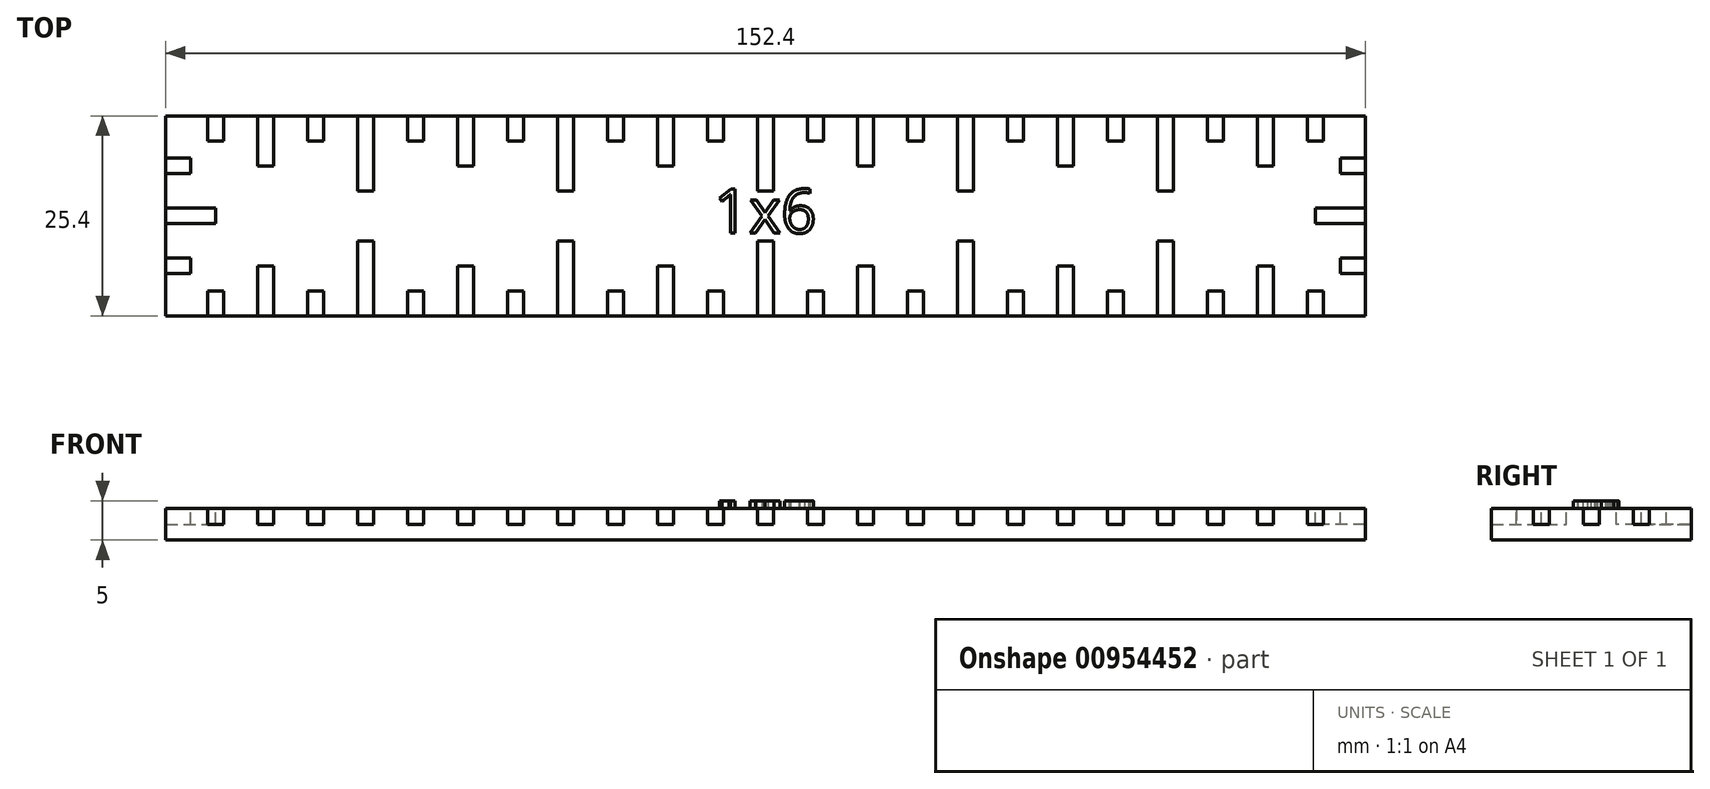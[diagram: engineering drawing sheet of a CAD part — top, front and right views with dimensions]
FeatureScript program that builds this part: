
annotation { "Feature Type Name" : "Feature", "Feature Type Description" : "" }
export const myFeature = defineFeature(function(context is Context, id is Id, definition is map)
    precondition{}
    {
        {
            var Q0;
            Q0=qCreatedBy(makeId("Top.planeOp"),FACE);
            var sketch = newSketch(context, id + "F0", { "sketchPlane" : qUnion([Q0])});
            skLineSegment(sketch, "E0.bottom", {"start": v(-76.2, 12.7) * mm, "end": v(76.2, 12.7) * mm});
            skLineSegment(sketch, "E0.top", {"start": v(-76.2, -12.7) * mm, "end": v(76.2, -12.7) * mm});
            skLineSegment(sketch, "E0.left", {"start": v(-76.2, 12.7) * mm, "end": v(-76.2, -12.7) * mm});
            skLineSegment(sketch, "E0.right", {"start": v(76.2, 12.7) * mm, "end": v(76.2, -12.7) * mm});
            skPoint(sketch, "E0.middle", {"position": v(0, 0) * mm});
            skSolve(sketch);
        }
        {
            var Q0;
            Q0=makeQuery(id+"F0.imprint","IMPRINT",FACE,{"disambiguationData":[TD([[makeQuery(id+"F0.imprint","IMPRINT",EDGE,{"derivedFrom":sQuery(id+"F0.wireOp",EDGE,"E0.bottom")}),-1.0]])]});
            extrude(context, id + "F1", {"entities" : qUnion([Q0]), "depth" : 4 * mm, "offsetDistance" : 25 * mm});
        }
        {
            var Q0;
            Q0=makeQuery(id+"F1.opExtrude","CAP_FACE",FACE,{"disambiguationData":[OSD([sQuery(id+"F0.wireOp",EDGE,"E0.bottom"),sQuery(id+"F0.wireOp",EDGE,"E0.top"),sQuery(id+"F0.wireOp",EDGE,"E0.left"),sQuery(id+"F0.wireOp",EDGE,"E0.right")])],"isStart":false});
            var sketch = newSketch(context, id + "F2", { "sketchPlane" : qUnion([Q0])});
            skLineSegment(sketch, "E1.bottom", {"start": v(-1, -3.17) * mm, "end": v(1, -3.17) * mm});
            skLineSegment(sketch, "E1.top", {"start": v(-1, -22.23) * mm, "end": v(1, -22.23) * mm});
            skLineSegment(sketch, "E1.left", {"start": v(-1, -3.17) * mm, "end": v(-1, -22.23) * mm});
            skLineSegment(sketch, "E1.right", {"start": v(1, -3.17) * mm, "end": v(1, -22.23) * mm});
            skPoint(sketch, "E1.middle", {"position": v(0, -12.7) * mm});
            skLineSegment(sketch, "E2.bottom", {"start": v(5.35, -9.53) * mm, "end": v(7.35, -9.53) * mm});
            skLineSegment(sketch, "E2.top", {"start": v(5.35, -15.88) * mm, "end": v(7.35, -15.88) * mm});
            skLineSegment(sketch, "E2.left", {"start": v(5.35, -9.53) * mm, "end": v(5.35, -15.88) * mm});
            skLineSegment(sketch, "E2.right", {"start": v(7.35, -9.53) * mm, "end": v(7.35, -15.88) * mm});
            skPoint(sketch, "E2.middle", {"position": v(6.35, -12.7) * mm});
            skLineSegment(sketch, "E3.bottom", {"start": v(-7.35, -9.53) * mm, "end": v(-5.35, -9.53) * mm});
            skLineSegment(sketch, "E3.top", {"start": v(-7.35, -15.88) * mm, "end": v(-5.35, -15.88) * mm});
            skLineSegment(sketch, "E3.left", {"start": v(-7.35, -9.53) * mm, "end": v(-7.35, -15.88) * mm});
            skLineSegment(sketch, "E3.right", {"start": v(-5.35, -9.53) * mm, "end": v(-5.35, -15.88) * mm});
            skPoint(sketch, "E3.middle", {"position": v(-6.35, -12.7) * mm});
            skLineSegment(sketch, "E4.bottom", {"start": v(-82.55, -1) * mm, "end": v(-82.55, 1) * mm});
            skLineSegment(sketch, "E4.top", {"start": v(-69.85, -1) * mm, "end": v(-69.85, 1) * mm});
            skLineSegment(sketch, "E4.left", {"start": v(-82.55, -1) * mm, "end": v(-69.85, -1) * mm});
            skLineSegment(sketch, "E4.right", {"start": v(-82.55, 1) * mm, "end": v(-69.85, 1) * mm});
            skPoint(sketch, "E4.middle", {"position": v(-76.2, 0) * mm});
            skLineSegment(sketch, "E5.bottom", {"start": v(-79.38, 5.35) * mm, "end": v(-79.38, 7.35) * mm});
            skLineSegment(sketch, "E5.top", {"start": v(-73.03, 5.35) * mm, "end": v(-73.03, 7.35) * mm});
            skLineSegment(sketch, "E5.left", {"start": v(-79.38, 5.35) * mm, "end": v(-73.03, 5.35) * mm});
            skLineSegment(sketch, "E5.right", {"start": v(-79.38, 7.35) * mm, "end": v(-73.03, 7.35) * mm});
            skPoint(sketch, "E5.middle", {"position": v(-76.2, 6.35) * mm});
            skLineSegment(sketch, "E6.bottom", {"start": v(-79.38, -7.35) * mm, "end": v(-79.38, -5.35) * mm});
            skLineSegment(sketch, "E6.top", {"start": v(-73.03, -7.35) * mm, "end": v(-73.03, -5.35) * mm});
            skLineSegment(sketch, "E6.left", {"start": v(-79.38, -7.35) * mm, "end": v(-73.03, -7.35) * mm});
            skLineSegment(sketch, "E6.right", {"start": v(-79.38, -5.35) * mm, "end": v(-73.03, -5.35) * mm});
            skPoint(sketch, "E6.middle", {"position": v(-76.2, -6.35) * mm});
            skLineSegment(sketch, "E7.bottom", {"start": v(1, 3.17) * mm, "end": v(-1, 3.17) * mm});
            skLineSegment(sketch, "E7.top", {"start": v(1, 22.22) * mm, "end": v(-1, 22.22) * mm});
            skLineSegment(sketch, "E7.left", {"start": v(1, 3.17) * mm, "end": v(1, 22.22) * mm});
            skLineSegment(sketch, "E7.right", {"start": v(-1, 3.17) * mm, "end": v(-1, 22.22) * mm});
            skPoint(sketch, "E7.middle", {"position": v(0, 12.7) * mm});
            skLineSegment(sketch, "E8.bottom", {"start": v(-5.35, 9.53) * mm, "end": v(-7.35, 9.53) * mm});
            skLineSegment(sketch, "E8.top", {"start": v(-5.35, 15.88) * mm, "end": v(-7.35, 15.88) * mm});
            skLineSegment(sketch, "E8.left", {"start": v(-5.35, 9.53) * mm, "end": v(-5.35, 15.88) * mm});
            skLineSegment(sketch, "E8.right", {"start": v(-7.35, 9.53) * mm, "end": v(-7.35, 15.88) * mm});
            skPoint(sketch, "E8.middle", {"position": v(-6.35, 12.7) * mm});
            skLineSegment(sketch, "E9.bottom", {"start": v(7.35, 9.52) * mm, "end": v(5.35, 9.52) * mm});
            skLineSegment(sketch, "E9.top", {"start": v(7.35, 15.88) * mm, "end": v(5.35, 15.88) * mm});
            skLineSegment(sketch, "E9.left", {"start": v(7.35, 9.52) * mm, "end": v(7.35, 15.88) * mm});
            skLineSegment(sketch, "E9.right", {"start": v(5.35, 9.52) * mm, "end": v(5.35, 15.88) * mm});
            skPoint(sketch, "E9.middle", {"position": v(6.35, 12.7) * mm});
            skLineSegment(sketch, "E10.bottom", {"start": v(82.55, 1) * mm, "end": v(82.55, -1) * mm});
            skLineSegment(sketch, "E10.top", {"start": v(69.85, 1) * mm, "end": v(69.85, -1) * mm});
            skLineSegment(sketch, "E10.left", {"start": v(82.55, 1) * mm, "end": v(69.85, 1) * mm});
            skLineSegment(sketch, "E10.right", {"start": v(82.55, -1) * mm, "end": v(69.85, -1) * mm});
            skPoint(sketch, "E10.middle", {"position": v(76.2, 0) * mm});
            skLineSegment(sketch, "E11.bottom", {"start": v(79.38, -5.35) * mm, "end": v(79.38, -7.35) * mm});
            skLineSegment(sketch, "E11.top", {"start": v(73.03, -5.35) * mm, "end": v(73.03, -7.35) * mm});
            skLineSegment(sketch, "E11.left", {"start": v(79.38, -5.35) * mm, "end": v(73.03, -5.35) * mm});
            skLineSegment(sketch, "E11.right", {"start": v(79.38, -7.35) * mm, "end": v(73.03, -7.35) * mm});
            skPoint(sketch, "E11.middle", {"position": v(76.2, -6.35) * mm});
            skLineSegment(sketch, "E12.bottom", {"start": v(79.38, 7.35) * mm, "end": v(79.38, 5.35) * mm});
            skLineSegment(sketch, "E12.top", {"start": v(73.03, 7.35) * mm, "end": v(73.03, 5.35) * mm});
            skLineSegment(sketch, "E12.left", {"start": v(79.38, 7.35) * mm, "end": v(73.03, 7.35) * mm});
            skLineSegment(sketch, "E12.right", {"start": v(79.38, 5.35) * mm, "end": v(73.03, 5.35) * mm});
            skPoint(sketch, "E12.middle", {"position": v(76.2, 6.35) * mm});
            skLineSegment(sketch, "E13.bottom", {"start": v(-11.7, 6.35) * mm, "end": v(-13.7, 6.35) * mm});
            skLineSegment(sketch, "E13.top", {"start": v(-11.7, 19.05) * mm, "end": v(-13.7, 19.05) * mm});
            skLineSegment(sketch, "E13.left", {"start": v(-11.7, 6.35) * mm, "end": v(-11.7, 19.05) * mm});
            skLineSegment(sketch, "E13.right", {"start": v(-13.7, 6.35) * mm, "end": v(-13.7, 19.05) * mm});
            skPoint(sketch, "E13.middle", {"position": v(-12.7, 12.7) * mm});
            skLineSegment(sketch, "E14.bottom", {"start": v(-18.05, 9.53) * mm, "end": v(-20.05, 9.53) * mm});
            skLineSegment(sketch, "E14.top", {"start": v(-18.05, 15.88) * mm, "end": v(-20.05, 15.88) * mm});
            skLineSegment(sketch, "E14.left", {"start": v(-18.05, 9.53) * mm, "end": v(-18.05, 15.88) * mm});
            skLineSegment(sketch, "E14.right", {"start": v(-20.05, 9.53) * mm, "end": v(-20.05, 15.88) * mm});
            skPoint(sketch, "E14.middle", {"position": v(-19.05, 12.7) * mm});
            skLineSegment(sketch, "E15.bottom", {"start": v(-11.7, -19.05) * mm, "end": v(-13.7, -19.05) * mm});
            skLineSegment(sketch, "E15.top", {"start": v(-11.7, -6.35) * mm, "end": v(-13.7, -6.35) * mm});
            skLineSegment(sketch, "E15.left", {"start": v(-11.7, -19.05) * mm, "end": v(-11.7, -6.35) * mm});
            skLineSegment(sketch, "E15.right", {"start": v(-13.7, -19.05) * mm, "end": v(-13.7, -6.35) * mm});
            skPoint(sketch, "E15.middle", {"position": v(-12.7, -12.7) * mm});
            skLineSegment(sketch, "E16.bottom", {"start": v(-18.05, -15.88) * mm, "end": v(-20.05, -15.88) * mm});
            skLineSegment(sketch, "E16.top", {"start": v(-18.05, -9.53) * mm, "end": v(-20.05, -9.53) * mm});
            skLineSegment(sketch, "E16.left", {"start": v(-18.05, -15.88) * mm, "end": v(-18.05, -9.53) * mm});
            skLineSegment(sketch, "E16.right", {"start": v(-20.05, -15.88) * mm, "end": v(-20.05, -9.53) * mm});
            skPoint(sketch, "E16.middle", {"position": v(-19.05, -12.7) * mm});
            skLineSegment(sketch, "E17.bottom", {"start": v(-5.35, -15.88) * mm, "end": v(-7.35, -15.88) * mm});
            skLineSegment(sketch, "E17.top", {"start": v(-5.35, -9.53) * mm, "end": v(-7.35, -9.53) * mm});
            skLineSegment(sketch, "E17.left", {"start": v(-5.35, -15.88) * mm, "end": v(-5.35, -9.53) * mm});
            skLineSegment(sketch, "E17.right", {"start": v(-7.35, -15.88) * mm, "end": v(-7.35, -9.53) * mm});
            skLineSegment(sketch, "E18.bottom", {"start": v(11.7, -6.35) * mm, "end": v(13.7, -6.35) * mm});
            skLineSegment(sketch, "E18.top", {"start": v(11.7, -19.05) * mm, "end": v(13.7, -19.05) * mm});
            skLineSegment(sketch, "E18.left", {"start": v(11.7, -6.35) * mm, "end": v(11.7, -19.05) * mm});
            skLineSegment(sketch, "E18.right", {"start": v(13.7, -6.35) * mm, "end": v(13.7, -19.05) * mm});
            skPoint(sketch, "E18.middle", {"position": v(12.7, -12.7) * mm});
            skLineSegment(sketch, "E19.bottom", {"start": v(18.05, -9.53) * mm, "end": v(20.05, -9.53) * mm});
            skLineSegment(sketch, "E19.top", {"start": v(18.05, -15.88) * mm, "end": v(20.05, -15.88) * mm});
            skLineSegment(sketch, "E19.left", {"start": v(18.05, -9.53) * mm, "end": v(18.05, -15.88) * mm});
            skLineSegment(sketch, "E19.right", {"start": v(20.05, -9.53) * mm, "end": v(20.05, -15.88) * mm});
            skPoint(sketch, "E19.middle", {"position": v(19.05, -12.7) * mm});
            skLineSegment(sketch, "E20.bottom", {"start": v(11.7, 19.05) * mm, "end": v(13.7, 19.05) * mm});
            skLineSegment(sketch, "E20.top", {"start": v(11.7, 6.35) * mm, "end": v(13.7, 6.35) * mm});
            skLineSegment(sketch, "E20.left", {"start": v(11.7, 19.05) * mm, "end": v(11.7, 6.35) * mm});
            skLineSegment(sketch, "E20.right", {"start": v(13.7, 19.05) * mm, "end": v(13.7, 6.35) * mm});
            skPoint(sketch, "E20.middle", {"position": v(12.7, 12.7) * mm});
            skLineSegment(sketch, "E21.bottom", {"start": v(18.05, 15.88) * mm, "end": v(20.05, 15.88) * mm});
            skLineSegment(sketch, "E21.top", {"start": v(18.05, 9.53) * mm, "end": v(20.05, 9.53) * mm});
            skLineSegment(sketch, "E21.left", {"start": v(18.05, 15.88) * mm, "end": v(18.05, 9.53) * mm});
            skLineSegment(sketch, "E21.right", {"start": v(20.05, 15.88) * mm, "end": v(20.05, 9.53) * mm});
            skPoint(sketch, "E21.middle", {"position": v(19.05, 12.7) * mm});
            skLineSegment(sketch, "E22.bottom", {"start": v(5.35, 15.88) * mm, "end": v(7.35, 15.88) * mm});
            skLineSegment(sketch, "E22.top", {"start": v(5.35, 9.53) * mm, "end": v(7.35, 9.53) * mm});
            skLineSegment(sketch, "E22.left", {"start": v(5.35, 15.88) * mm, "end": v(5.35, 9.53) * mm});
            skLineSegment(sketch, "E22.right", {"start": v(7.35, 15.88) * mm, "end": v(7.35, 9.53) * mm});
            skLineSegment(sketch, "E23.bottom", {"start": v(26.4, 3.17) * mm, "end": v(24.4, 3.17) * mm});
            skLineSegment(sketch, "E23.top", {"start": v(26.4, 22.22) * mm, "end": v(24.4, 22.22) * mm});
            skLineSegment(sketch, "E23.left", {"start": v(26.4, 3.17) * mm, "end": v(26.4, 22.22) * mm});
            skLineSegment(sketch, "E23.right", {"start": v(24.4, 3.17) * mm, "end": v(24.4, 22.22) * mm});
            skPoint(sketch, "E23.middle", {"position": v(25.4, 12.7) * mm});
            skLineSegment(sketch, "E24.bottom", {"start": v(20.05, 9.52) * mm, "end": v(18.05, 9.52) * mm});
            skLineSegment(sketch, "E24.top", {"start": v(20.05, 15.87) * mm, "end": v(18.05, 15.87) * mm});
            skLineSegment(sketch, "E24.left", {"start": v(20.05, 9.52) * mm, "end": v(20.05, 15.87) * mm});
            skLineSegment(sketch, "E24.right", {"start": v(18.05, 9.52) * mm, "end": v(18.05, 15.87) * mm});
            skLineSegment(sketch, "E25.bottom", {"start": v(32.75, 9.52) * mm, "end": v(30.75, 9.52) * mm});
            skLineSegment(sketch, "E25.top", {"start": v(32.75, 15.87) * mm, "end": v(30.75, 15.87) * mm});
            skLineSegment(sketch, "E25.left", {"start": v(32.75, 9.52) * mm, "end": v(32.75, 15.87) * mm});
            skLineSegment(sketch, "E25.right", {"start": v(30.75, 9.52) * mm, "end": v(30.75, 15.87) * mm});
            skPoint(sketch, "E25.middle", {"position": v(31.75, 12.7) * mm});
            skLineSegment(sketch, "E26.bottom", {"start": v(20.05, 9.53) * mm, "end": v(18.05, 9.53) * mm});
            skLineSegment(sketch, "E26.top", {"start": v(20.05, 15.88) * mm, "end": v(18.05, 15.88) * mm});
            skLineSegment(sketch, "E26.left", {"start": v(20.05, 9.53) * mm, "end": v(20.05, 15.88) * mm});
            skLineSegment(sketch, "E26.right", {"start": v(18.05, 9.53) * mm, "end": v(18.05, 15.88) * mm});
            skLineSegment(sketch, "E27.bottom", {"start": v(37.1, 19.05) * mm, "end": v(39.1, 19.05) * mm});
            skLineSegment(sketch, "E27.top", {"start": v(37.1, 6.35) * mm, "end": v(39.1, 6.35) * mm});
            skLineSegment(sketch, "E27.left", {"start": v(37.1, 19.05) * mm, "end": v(37.1, 6.35) * mm});
            skLineSegment(sketch, "E27.right", {"start": v(39.1, 19.05) * mm, "end": v(39.1, 6.35) * mm});
            skPoint(sketch, "E27.middle", {"position": v(38.1, 12.7) * mm});
            skLineSegment(sketch, "E28.bottom", {"start": v(43.45, 15.87) * mm, "end": v(45.45, 15.87) * mm});
            skLineSegment(sketch, "E28.top", {"start": v(43.45, 9.52) * mm, "end": v(45.45, 9.52) * mm});
            skLineSegment(sketch, "E28.left", {"start": v(43.45, 15.87) * mm, "end": v(43.45, 9.52) * mm});
            skLineSegment(sketch, "E28.right", {"start": v(45.45, 15.87) * mm, "end": v(45.45, 9.52) * mm});
            skPoint(sketch, "E28.middle", {"position": v(44.45, 12.7) * mm});
            skLineSegment(sketch, "E29.bottom", {"start": v(30.75, 15.87) * mm, "end": v(32.75, 15.87) * mm});
            skLineSegment(sketch, "E29.top", {"start": v(30.75, 9.52) * mm, "end": v(32.75, 9.52) * mm});
            skLineSegment(sketch, "E29.left", {"start": v(30.75, 15.87) * mm, "end": v(30.75, 9.52) * mm});
            skLineSegment(sketch, "E29.right", {"start": v(32.75, 15.87) * mm, "end": v(32.75, 9.52) * mm});
            skLineSegment(sketch, "E30.bottom", {"start": v(26.4, -22.22) * mm, "end": v(24.4, -22.22) * mm});
            skLineSegment(sketch, "E30.top", {"start": v(26.4, -3.17) * mm, "end": v(24.4, -3.17) * mm});
            skLineSegment(sketch, "E30.left", {"start": v(26.4, -22.22) * mm, "end": v(26.4, -3.17) * mm});
            skLineSegment(sketch, "E30.right", {"start": v(24.4, -22.22) * mm, "end": v(24.4, -3.17) * mm});
            skPoint(sketch, "E30.middle", {"position": v(25.4, -12.7) * mm});
            skLineSegment(sketch, "E31.bottom", {"start": v(20.05, -15.87) * mm, "end": v(18.05, -15.87) * mm});
            skLineSegment(sketch, "E31.top", {"start": v(20.05, -9.52) * mm, "end": v(18.05, -9.52) * mm});
            skLineSegment(sketch, "E31.left", {"start": v(20.05, -15.87) * mm, "end": v(20.05, -9.52) * mm});
            skLineSegment(sketch, "E31.right", {"start": v(18.05, -15.87) * mm, "end": v(18.05, -9.52) * mm});
            skLineSegment(sketch, "E32.bottom", {"start": v(32.75, -15.87) * mm, "end": v(30.75, -15.87) * mm});
            skLineSegment(sketch, "E32.top", {"start": v(32.75, -9.52) * mm, "end": v(30.75, -9.52) * mm});
            skLineSegment(sketch, "E32.left", {"start": v(32.75, -15.87) * mm, "end": v(32.75, -9.52) * mm});
            skLineSegment(sketch, "E32.right", {"start": v(30.75, -15.87) * mm, "end": v(30.75, -9.52) * mm});
            skPoint(sketch, "E32.middle", {"position": v(31.75, -12.7) * mm});
            skLineSegment(sketch, "E33.bottom", {"start": v(37.1, -6.35) * mm, "end": v(39.1, -6.35) * mm});
            skLineSegment(sketch, "E33.top", {"start": v(37.1, -19.05) * mm, "end": v(39.1, -19.05) * mm});
            skLineSegment(sketch, "E33.left", {"start": v(37.1, -6.35) * mm, "end": v(37.1, -19.05) * mm});
            skLineSegment(sketch, "E33.right", {"start": v(39.1, -6.35) * mm, "end": v(39.1, -19.05) * mm});
            skPoint(sketch, "E33.middle", {"position": v(38.1, -12.7) * mm});
            skLineSegment(sketch, "E34.bottom", {"start": v(43.45, -9.52) * mm, "end": v(45.45, -9.52) * mm});
            skLineSegment(sketch, "E34.top", {"start": v(43.45, -15.87) * mm, "end": v(45.45, -15.87) * mm});
            skLineSegment(sketch, "E34.left", {"start": v(43.45, -9.52) * mm, "end": v(43.45, -15.87) * mm});
            skLineSegment(sketch, "E34.right", {"start": v(45.45, -9.52) * mm, "end": v(45.45, -15.87) * mm});
            skPoint(sketch, "E34.middle", {"position": v(44.45, -12.7) * mm});
            skLineSegment(sketch, "E35.bottom", {"start": v(30.75, -9.52) * mm, "end": v(32.75, -9.52) * mm});
            skLineSegment(sketch, "E35.top", {"start": v(30.75, -15.87) * mm, "end": v(32.75, -15.87) * mm});
            skLineSegment(sketch, "E35.left", {"start": v(30.75, -9.52) * mm, "end": v(30.75, -15.87) * mm});
            skLineSegment(sketch, "E35.right", {"start": v(32.75, -9.52) * mm, "end": v(32.75, -15.87) * mm});
            skLineSegment(sketch, "E36.bottom", {"start": v(-26.4, -3.17) * mm, "end": v(-24.4, -3.17) * mm});
            skLineSegment(sketch, "E36.top", {"start": v(-26.4, -22.22) * mm, "end": v(-24.4, -22.22) * mm});
            skLineSegment(sketch, "E36.left", {"start": v(-26.4, -3.17) * mm, "end": v(-26.4, -22.22) * mm});
            skLineSegment(sketch, "E36.right", {"start": v(-24.4, -3.17) * mm, "end": v(-24.4, -22.22) * mm});
            skPoint(sketch, "E36.middle", {"position": v(-25.4, -12.7) * mm});
            skLineSegment(sketch, "E37.bottom", {"start": v(-20.05, -9.52) * mm, "end": v(-18.05, -9.52) * mm});
            skLineSegment(sketch, "E37.top", {"start": v(-20.05, -15.87) * mm, "end": v(-18.05, -15.87) * mm});
            skLineSegment(sketch, "E37.left", {"start": v(-20.05, -9.52) * mm, "end": v(-20.05, -15.87) * mm});
            skLineSegment(sketch, "E37.right", {"start": v(-18.05, -9.52) * mm, "end": v(-18.05, -15.87) * mm});
            skLineSegment(sketch, "E38.bottom", {"start": v(-32.75, -9.52) * mm, "end": v(-30.75, -9.52) * mm});
            skLineSegment(sketch, "E38.top", {"start": v(-32.75, -15.87) * mm, "end": v(-30.75, -15.87) * mm});
            skLineSegment(sketch, "E38.left", {"start": v(-32.75, -9.52) * mm, "end": v(-32.75, -15.87) * mm});
            skLineSegment(sketch, "E38.right", {"start": v(-30.75, -9.52) * mm, "end": v(-30.75, -15.87) * mm});
            skPoint(sketch, "E38.middle", {"position": v(-31.75, -12.7) * mm});
            skLineSegment(sketch, "E39.bottom", {"start": v(-20.05, -9.53) * mm, "end": v(-18.05, -9.53) * mm});
            skLineSegment(sketch, "E39.top", {"start": v(-20.05, -15.88) * mm, "end": v(-18.05, -15.88) * mm});
            skLineSegment(sketch, "E39.left", {"start": v(-20.05, -9.53) * mm, "end": v(-20.05, -15.88) * mm});
            skLineSegment(sketch, "E39.right", {"start": v(-18.05, -9.53) * mm, "end": v(-18.05, -15.88) * mm});
            skLineSegment(sketch, "E40.bottom", {"start": v(-37.1, -19.05) * mm, "end": v(-39.1, -19.05) * mm});
            skLineSegment(sketch, "E40.top", {"start": v(-37.1, -6.35) * mm, "end": v(-39.1, -6.35) * mm});
            skLineSegment(sketch, "E40.left", {"start": v(-37.1, -19.05) * mm, "end": v(-37.1, -6.35) * mm});
            skLineSegment(sketch, "E40.right", {"start": v(-39.1, -19.05) * mm, "end": v(-39.1, -6.35) * mm});
            skPoint(sketch, "E40.middle", {"position": v(-38.1, -12.7) * mm});
            skLineSegment(sketch, "E41.bottom", {"start": v(-43.45, -15.87) * mm, "end": v(-45.45, -15.87) * mm});
            skLineSegment(sketch, "E41.top", {"start": v(-43.45, -9.52) * mm, "end": v(-45.45, -9.52) * mm});
            skLineSegment(sketch, "E41.left", {"start": v(-43.45, -15.87) * mm, "end": v(-43.45, -9.52) * mm});
            skLineSegment(sketch, "E41.right", {"start": v(-45.45, -15.87) * mm, "end": v(-45.45, -9.52) * mm});
            skPoint(sketch, "E41.middle", {"position": v(-44.45, -12.7) * mm});
            skLineSegment(sketch, "E42.bottom", {"start": v(-30.75, -15.87) * mm, "end": v(-32.75, -15.87) * mm});
            skLineSegment(sketch, "E42.top", {"start": v(-30.75, -9.52) * mm, "end": v(-32.75, -9.52) * mm});
            skLineSegment(sketch, "E42.left", {"start": v(-30.75, -15.87) * mm, "end": v(-30.75, -9.52) * mm});
            skLineSegment(sketch, "E42.right", {"start": v(-32.75, -15.87) * mm, "end": v(-32.75, -9.52) * mm});
            skLineSegment(sketch, "E43.bottom", {"start": v(-26.4, 22.22) * mm, "end": v(-24.4, 22.22) * mm});
            skLineSegment(sketch, "E43.top", {"start": v(-26.4, 3.17) * mm, "end": v(-24.4, 3.17) * mm});
            skLineSegment(sketch, "E43.left", {"start": v(-26.4, 22.22) * mm, "end": v(-26.4, 3.17) * mm});
            skLineSegment(sketch, "E43.right", {"start": v(-24.4, 22.22) * mm, "end": v(-24.4, 3.17) * mm});
            skPoint(sketch, "E43.middle", {"position": v(-25.4, 12.7) * mm});
            skLineSegment(sketch, "E44.bottom", {"start": v(-20.05, 15.87) * mm, "end": v(-18.05, 15.87) * mm});
            skLineSegment(sketch, "E44.top", {"start": v(-20.05, 9.52) * mm, "end": v(-18.05, 9.52) * mm});
            skLineSegment(sketch, "E44.left", {"start": v(-20.05, 15.87) * mm, "end": v(-20.05, 9.52) * mm});
            skLineSegment(sketch, "E44.right", {"start": v(-18.05, 15.87) * mm, "end": v(-18.05, 9.52) * mm});
            skLineSegment(sketch, "E45.bottom", {"start": v(-32.75, 15.87) * mm, "end": v(-30.75, 15.87) * mm});
            skLineSegment(sketch, "E45.top", {"start": v(-32.75, 9.52) * mm, "end": v(-30.75, 9.52) * mm});
            skLineSegment(sketch, "E45.left", {"start": v(-32.75, 15.87) * mm, "end": v(-32.75, 9.52) * mm});
            skLineSegment(sketch, "E45.right", {"start": v(-30.75, 15.87) * mm, "end": v(-30.75, 9.52) * mm});
            skPoint(sketch, "E45.middle", {"position": v(-31.75, 12.7) * mm});
            skLineSegment(sketch, "E46.bottom", {"start": v(-37.1, 6.35) * mm, "end": v(-39.1, 6.35) * mm});
            skLineSegment(sketch, "E46.top", {"start": v(-37.1, 19.05) * mm, "end": v(-39.1, 19.05) * mm});
            skLineSegment(sketch, "E46.left", {"start": v(-37.1, 6.35) * mm, "end": v(-37.1, 19.05) * mm});
            skLineSegment(sketch, "E46.right", {"start": v(-39.1, 6.35) * mm, "end": v(-39.1, 19.05) * mm});
            skPoint(sketch, "E46.middle", {"position": v(-38.1, 12.7) * mm});
            skLineSegment(sketch, "E47.bottom", {"start": v(-43.45, 9.52) * mm, "end": v(-45.45, 9.52) * mm});
            skLineSegment(sketch, "E47.top", {"start": v(-43.45, 15.87) * mm, "end": v(-45.45, 15.87) * mm});
            skLineSegment(sketch, "E47.left", {"start": v(-43.45, 9.52) * mm, "end": v(-43.45, 15.87) * mm});
            skLineSegment(sketch, "E47.right", {"start": v(-45.45, 9.52) * mm, "end": v(-45.45, 15.87) * mm});
            skPoint(sketch, "E47.middle", {"position": v(-44.45, 12.7) * mm});
            skLineSegment(sketch, "E48.bottom", {"start": v(-30.75, 9.52) * mm, "end": v(-32.75, 9.52) * mm});
            skLineSegment(sketch, "E48.top", {"start": v(-30.75, 15.87) * mm, "end": v(-32.75, 15.87) * mm});
            skLineSegment(sketch, "E48.left", {"start": v(-30.75, 9.52) * mm, "end": v(-30.75, 15.87) * mm});
            skLineSegment(sketch, "E48.right", {"start": v(-32.75, 9.52) * mm, "end": v(-32.75, 15.87) * mm});
            skLineSegment(sketch, "E49.bottom", {"start": v(43.45, 15.88) * mm, "end": v(45.45, 15.88) * mm});
            skLineSegment(sketch, "E49.top", {"start": v(43.45, 9.53) * mm, "end": v(45.45, 9.53) * mm});
            skLineSegment(sketch, "E49.left", {"start": v(43.45, 15.88) * mm, "end": v(43.45, 9.53) * mm});
            skLineSegment(sketch, "E49.right", {"start": v(45.45, 15.88) * mm, "end": v(45.45, 9.53) * mm});
            skLineSegment(sketch, "E50.bottom", {"start": v(51.8, 3.17) * mm, "end": v(49.8, 3.17) * mm});
            skLineSegment(sketch, "E50.top", {"start": v(51.8, 22.22) * mm, "end": v(49.8, 22.22) * mm});
            skLineSegment(sketch, "E50.left", {"start": v(51.8, 3.17) * mm, "end": v(51.8, 22.22) * mm});
            skLineSegment(sketch, "E50.right", {"start": v(49.8, 3.17) * mm, "end": v(49.8, 22.22) * mm});
            skPoint(sketch, "E50.middle", {"position": v(50.8, 12.7) * mm});
            skLineSegment(sketch, "E51.bottom", {"start": v(45.45, 9.52) * mm, "end": v(43.45, 9.52) * mm});
            skLineSegment(sketch, "E51.top", {"start": v(45.45, 15.87) * mm, "end": v(43.45, 15.87) * mm});
            skLineSegment(sketch, "E51.left", {"start": v(45.45, 9.52) * mm, "end": v(45.45, 15.87) * mm});
            skLineSegment(sketch, "E51.right", {"start": v(43.45, 9.52) * mm, "end": v(43.45, 15.87) * mm});
            skLineSegment(sketch, "E52.bottom", {"start": v(58.15, 9.52) * mm, "end": v(56.15, 9.52) * mm});
            skLineSegment(sketch, "E52.top", {"start": v(58.15, 15.87) * mm, "end": v(56.15, 15.87) * mm});
            skLineSegment(sketch, "E52.left", {"start": v(58.15, 9.52) * mm, "end": v(58.15, 15.87) * mm});
            skLineSegment(sketch, "E52.right", {"start": v(56.15, 9.52) * mm, "end": v(56.15, 15.87) * mm});
            skPoint(sketch, "E52.middle", {"position": v(57.15, 12.7) * mm});
            skLineSegment(sketch, "E53.bottom", {"start": v(45.45, 9.53) * mm, "end": v(43.45, 9.53) * mm});
            skLineSegment(sketch, "E53.top", {"start": v(45.45, 15.88) * mm, "end": v(43.45, 15.88) * mm});
            skLineSegment(sketch, "E53.left", {"start": v(45.45, 9.53) * mm, "end": v(45.45, 15.88) * mm});
            skLineSegment(sketch, "E53.right", {"start": v(43.45, 9.53) * mm, "end": v(43.45, 15.88) * mm});
            skLineSegment(sketch, "E54.bottom", {"start": v(62.5, 19.05) * mm, "end": v(64.5, 19.05) * mm});
            skLineSegment(sketch, "E54.top", {"start": v(62.5, 6.35) * mm, "end": v(64.5, 6.35) * mm});
            skLineSegment(sketch, "E54.left", {"start": v(62.5, 19.05) * mm, "end": v(62.5, 6.35) * mm});
            skLineSegment(sketch, "E54.right", {"start": v(64.5, 19.05) * mm, "end": v(64.5, 6.35) * mm});
            skPoint(sketch, "E54.middle", {"position": v(63.5, 12.7) * mm});
            skLineSegment(sketch, "E55.bottom", {"start": v(68.85, 15.87) * mm, "end": v(70.85, 15.87) * mm});
            skLineSegment(sketch, "E55.top", {"start": v(68.85, 9.52) * mm, "end": v(70.85, 9.52) * mm});
            skLineSegment(sketch, "E55.left", {"start": v(68.85, 15.87) * mm, "end": v(68.85, 9.52) * mm});
            skLineSegment(sketch, "E55.right", {"start": v(70.85, 15.87) * mm, "end": v(70.85, 9.52) * mm});
            skPoint(sketch, "E55.middle", {"position": v(69.85, 12.7) * mm});
            skLineSegment(sketch, "E56.bottom", {"start": v(56.15, 15.87) * mm, "end": v(58.15, 15.87) * mm});
            skLineSegment(sketch, "E56.top", {"start": v(56.15, 9.52) * mm, "end": v(58.15, 9.52) * mm});
            skLineSegment(sketch, "E56.left", {"start": v(56.15, 15.87) * mm, "end": v(56.15, 9.52) * mm});
            skLineSegment(sketch, "E56.right", {"start": v(58.15, 15.87) * mm, "end": v(58.15, 9.52) * mm});
            skLineSegment(sketch, "E57.bottom", {"start": v(51.8, -22.22) * mm, "end": v(49.8, -22.22) * mm});
            skLineSegment(sketch, "E57.top", {"start": v(51.8, -3.17) * mm, "end": v(49.8, -3.17) * mm});
            skLineSegment(sketch, "E57.left", {"start": v(51.8, -22.22) * mm, "end": v(51.8, -3.17) * mm});
            skLineSegment(sketch, "E57.right", {"start": v(49.8, -22.22) * mm, "end": v(49.8, -3.17) * mm});
            skPoint(sketch, "E57.middle", {"position": v(50.8, -12.7) * mm});
            skLineSegment(sketch, "E58.bottom", {"start": v(45.45, -15.87) * mm, "end": v(43.45, -15.87) * mm});
            skLineSegment(sketch, "E58.top", {"start": v(45.45, -9.52) * mm, "end": v(43.45, -9.52) * mm});
            skLineSegment(sketch, "E58.left", {"start": v(45.45, -15.87) * mm, "end": v(45.45, -9.52) * mm});
            skLineSegment(sketch, "E58.right", {"start": v(43.45, -15.87) * mm, "end": v(43.45, -9.52) * mm});
            skLineSegment(sketch, "E59.bottom", {"start": v(58.15, -15.87) * mm, "end": v(56.15, -15.87) * mm});
            skLineSegment(sketch, "E59.top", {"start": v(58.15, -9.52) * mm, "end": v(56.15, -9.52) * mm});
            skLineSegment(sketch, "E59.left", {"start": v(58.15, -15.87) * mm, "end": v(58.15, -9.52) * mm});
            skLineSegment(sketch, "E59.right", {"start": v(56.15, -15.87) * mm, "end": v(56.15, -9.52) * mm});
            skPoint(sketch, "E59.middle", {"position": v(57.15, -12.7) * mm});
            skLineSegment(sketch, "E60.bottom", {"start": v(62.5, -6.35) * mm, "end": v(64.5, -6.35) * mm});
            skLineSegment(sketch, "E60.top", {"start": v(62.5, -19.05) * mm, "end": v(64.5, -19.05) * mm});
            skLineSegment(sketch, "E60.left", {"start": v(62.5, -6.35) * mm, "end": v(62.5, -19.05) * mm});
            skLineSegment(sketch, "E60.right", {"start": v(64.5, -6.35) * mm, "end": v(64.5, -19.05) * mm});
            skPoint(sketch, "E60.middle", {"position": v(63.5, -12.7) * mm});
            skLineSegment(sketch, "E61.bottom", {"start": v(68.85, -9.52) * mm, "end": v(70.85, -9.52) * mm});
            skLineSegment(sketch, "E61.top", {"start": v(68.85, -15.87) * mm, "end": v(70.85, -15.87) * mm});
            skLineSegment(sketch, "E61.left", {"start": v(68.85, -9.52) * mm, "end": v(68.85, -15.87) * mm});
            skLineSegment(sketch, "E61.right", {"start": v(70.85, -9.52) * mm, "end": v(70.85, -15.87) * mm});
            skPoint(sketch, "E61.middle", {"position": v(69.85, -12.7) * mm});
            skLineSegment(sketch, "E62.bottom", {"start": v(56.15, -9.52) * mm, "end": v(58.15, -9.52) * mm});
            skLineSegment(sketch, "E62.top", {"start": v(56.15, -15.87) * mm, "end": v(58.15, -15.87) * mm});
            skLineSegment(sketch, "E62.left", {"start": v(56.15, -9.52) * mm, "end": v(56.15, -15.87) * mm});
            skLineSegment(sketch, "E62.right", {"start": v(58.15, -9.52) * mm, "end": v(58.15, -15.87) * mm});
            skLineSegment(sketch, "E63.bottom", {"start": v(-43.45, -15.88) * mm, "end": v(-45.45, -15.88) * mm});
            skLineSegment(sketch, "E63.top", {"start": v(-43.45, -9.53) * mm, "end": v(-45.45, -9.53) * mm});
            skLineSegment(sketch, "E63.left", {"start": v(-43.45, -15.88) * mm, "end": v(-43.45, -9.53) * mm});
            skLineSegment(sketch, "E63.right", {"start": v(-45.45, -15.88) * mm, "end": v(-45.45, -9.53) * mm});
            skLineSegment(sketch, "E64.bottom", {"start": v(-51.8, -3.17) * mm, "end": v(-49.8, -3.17) * mm});
            skLineSegment(sketch, "E64.top", {"start": v(-51.8, -22.22) * mm, "end": v(-49.8, -22.22) * mm});
            skLineSegment(sketch, "E64.left", {"start": v(-51.8, -3.17) * mm, "end": v(-51.8, -22.22) * mm});
            skLineSegment(sketch, "E64.right", {"start": v(-49.8, -3.17) * mm, "end": v(-49.8, -22.22) * mm});
            skPoint(sketch, "E64.middle", {"position": v(-50.8, -12.7) * mm});
            skLineSegment(sketch, "E65.bottom", {"start": v(-45.45, -9.52) * mm, "end": v(-43.45, -9.52) * mm});
            skLineSegment(sketch, "E65.top", {"start": v(-45.45, -15.87) * mm, "end": v(-43.45, -15.87) * mm});
            skLineSegment(sketch, "E65.left", {"start": v(-45.45, -9.52) * mm, "end": v(-45.45, -15.87) * mm});
            skLineSegment(sketch, "E65.right", {"start": v(-43.45, -9.52) * mm, "end": v(-43.45, -15.87) * mm});
            skLineSegment(sketch, "E66.bottom", {"start": v(-58.15, -9.52) * mm, "end": v(-56.15, -9.52) * mm});
            skLineSegment(sketch, "E66.top", {"start": v(-58.15, -15.87) * mm, "end": v(-56.15, -15.87) * mm});
            skLineSegment(sketch, "E66.left", {"start": v(-58.15, -9.52) * mm, "end": v(-58.15, -15.87) * mm});
            skLineSegment(sketch, "E66.right", {"start": v(-56.15, -9.52) * mm, "end": v(-56.15, -15.87) * mm});
            skPoint(sketch, "E66.middle", {"position": v(-57.15, -12.7) * mm});
            skLineSegment(sketch, "E67.bottom", {"start": v(-45.45, -9.53) * mm, "end": v(-43.45, -9.53) * mm});
            skLineSegment(sketch, "E67.top", {"start": v(-45.45, -15.88) * mm, "end": v(-43.45, -15.88) * mm});
            skLineSegment(sketch, "E67.left", {"start": v(-45.45, -9.53) * mm, "end": v(-45.45, -15.88) * mm});
            skLineSegment(sketch, "E67.right", {"start": v(-43.45, -9.53) * mm, "end": v(-43.45, -15.88) * mm});
            skLineSegment(sketch, "E68.bottom", {"start": v(-62.5, -19.05) * mm, "end": v(-64.5, -19.05) * mm});
            skLineSegment(sketch, "E68.top", {"start": v(-62.5, -6.35) * mm, "end": v(-64.5, -6.35) * mm});
            skLineSegment(sketch, "E68.left", {"start": v(-62.5, -19.05) * mm, "end": v(-62.5, -6.35) * mm});
            skLineSegment(sketch, "E68.right", {"start": v(-64.5, -19.05) * mm, "end": v(-64.5, -6.35) * mm});
            skPoint(sketch, "E68.middle", {"position": v(-63.5, -12.7) * mm});
            skLineSegment(sketch, "E69.bottom", {"start": v(-68.85, -15.87) * mm, "end": v(-70.85, -15.87) * mm});
            skLineSegment(sketch, "E69.top", {"start": v(-68.85, -9.52) * mm, "end": v(-70.85, -9.52) * mm});
            skLineSegment(sketch, "E69.left", {"start": v(-68.85, -15.87) * mm, "end": v(-68.85, -9.52) * mm});
            skLineSegment(sketch, "E69.right", {"start": v(-70.85, -15.87) * mm, "end": v(-70.85, -9.52) * mm});
            skPoint(sketch, "E69.middle", {"position": v(-69.85, -12.7) * mm});
            skLineSegment(sketch, "E70.bottom", {"start": v(-56.15, -15.87) * mm, "end": v(-58.15, -15.87) * mm});
            skLineSegment(sketch, "E70.top", {"start": v(-56.15, -9.52) * mm, "end": v(-58.15, -9.52) * mm});
            skLineSegment(sketch, "E70.left", {"start": v(-56.15, -15.87) * mm, "end": v(-56.15, -9.52) * mm});
            skLineSegment(sketch, "E70.right", {"start": v(-58.15, -15.87) * mm, "end": v(-58.15, -9.52) * mm});
            skLineSegment(sketch, "E71.bottom", {"start": v(-51.8, 22.22) * mm, "end": v(-49.8, 22.22) * mm});
            skLineSegment(sketch, "E71.top", {"start": v(-51.8, 3.17) * mm, "end": v(-49.8, 3.17) * mm});
            skLineSegment(sketch, "E71.left", {"start": v(-51.8, 22.22) * mm, "end": v(-51.8, 3.17) * mm});
            skLineSegment(sketch, "E71.right", {"start": v(-49.8, 22.22) * mm, "end": v(-49.8, 3.17) * mm});
            skPoint(sketch, "E71.middle", {"position": v(-50.8, 12.7) * mm});
            skLineSegment(sketch, "E72.bottom", {"start": v(-45.45, 15.87) * mm, "end": v(-43.45, 15.87) * mm});
            skLineSegment(sketch, "E72.top", {"start": v(-45.45, 9.52) * mm, "end": v(-43.45, 9.52) * mm});
            skLineSegment(sketch, "E72.left", {"start": v(-45.45, 15.87) * mm, "end": v(-45.45, 9.52) * mm});
            skLineSegment(sketch, "E72.right", {"start": v(-43.45, 15.87) * mm, "end": v(-43.45, 9.52) * mm});
            skLineSegment(sketch, "E73.bottom", {"start": v(-58.15, 15.87) * mm, "end": v(-56.15, 15.87) * mm});
            skLineSegment(sketch, "E73.top", {"start": v(-58.15, 9.52) * mm, "end": v(-56.15, 9.52) * mm});
            skLineSegment(sketch, "E73.left", {"start": v(-58.15, 15.87) * mm, "end": v(-58.15, 9.52) * mm});
            skLineSegment(sketch, "E73.right", {"start": v(-56.15, 15.87) * mm, "end": v(-56.15, 9.52) * mm});
            skPoint(sketch, "E73.middle", {"position": v(-57.15, 12.7) * mm});
            skLineSegment(sketch, "E74.bottom", {"start": v(-62.5, 6.35) * mm, "end": v(-64.5, 6.35) * mm});
            skLineSegment(sketch, "E74.top", {"start": v(-62.5, 19.05) * mm, "end": v(-64.5, 19.05) * mm});
            skLineSegment(sketch, "E74.left", {"start": v(-62.5, 6.35) * mm, "end": v(-62.5, 19.05) * mm});
            skLineSegment(sketch, "E74.right", {"start": v(-64.5, 6.35) * mm, "end": v(-64.5, 19.05) * mm});
            skPoint(sketch, "E74.middle", {"position": v(-63.5, 12.7) * mm});
            skLineSegment(sketch, "E75.bottom", {"start": v(-68.85, 9.52) * mm, "end": v(-70.85, 9.52) * mm});
            skLineSegment(sketch, "E75.top", {"start": v(-68.85, 15.87) * mm, "end": v(-70.85, 15.87) * mm});
            skLineSegment(sketch, "E75.left", {"start": v(-68.85, 9.52) * mm, "end": v(-68.85, 15.87) * mm});
            skLineSegment(sketch, "E75.right", {"start": v(-70.85, 9.52) * mm, "end": v(-70.85, 15.87) * mm});
            skPoint(sketch, "E75.middle", {"position": v(-69.85, 12.7) * mm});
            skLineSegment(sketch, "E76.bottom", {"start": v(-56.15, 9.52) * mm, "end": v(-58.15, 9.52) * mm});
            skLineSegment(sketch, "E76.top", {"start": v(-56.15, 15.87) * mm, "end": v(-58.15, 15.87) * mm});
            skLineSegment(sketch, "E76.left", {"start": v(-56.15, 9.52) * mm, "end": v(-56.15, 15.87) * mm});
            skLineSegment(sketch, "E76.right", {"start": v(-58.15, 9.52) * mm, "end": v(-58.15, 15.87) * mm});
            skSolve(sketch);
        }
        {
            var Q0;
            Q0=qSketchRegion(id+"F2",true);
            extrude(context, id + "F3", {"entities" : qUnion([Q0]), "operationType" : NewBodyOperationType.REMOVE, "oppositeDirection" : true, "depth" : 2 * mm, "offsetDistance" : 25 * mm});
        }
        {
            var Q0;
            Q0=makeQuery(id+"F1.opExtrude","CAP_FACE",FACE,{"disambiguationData":[OSD([sQuery(id+"F0.wireOp",EDGE,"E0.bottom"),sQuery(id+"F0.wireOp",EDGE,"E0.top"),sQuery(id+"F0.wireOp",EDGE,"E0.left"),sQuery(id+"F0.wireOp",EDGE,"E0.right")])],"isStart":false});
            var sketch = newSketch(context, id + "F4", { "sketchPlane" : qUnion([Q0])});
            skText(sketch, "E77", { "text": "1x6", "fontName": "OpenSans-Regular.ttf"});
            const initialGuessF4  = {"E77": [-0.00659, -0.0022, 1, 0, 0.00563]};
            skSetInitialGuess(sketch, initialGuessF4);
            skSolve(sketch);
        }
        {
            var Q0;
            Q0 = qSketchRegion(id + "F4", true);
            extrude(context, id + "F5", {"entities" : qUnion([Q0]), "operationType" : NewBodyOperationType.ADD, "depth" : 1 * mm, "offsetDistance" : 25 * mm});
        }
    });
